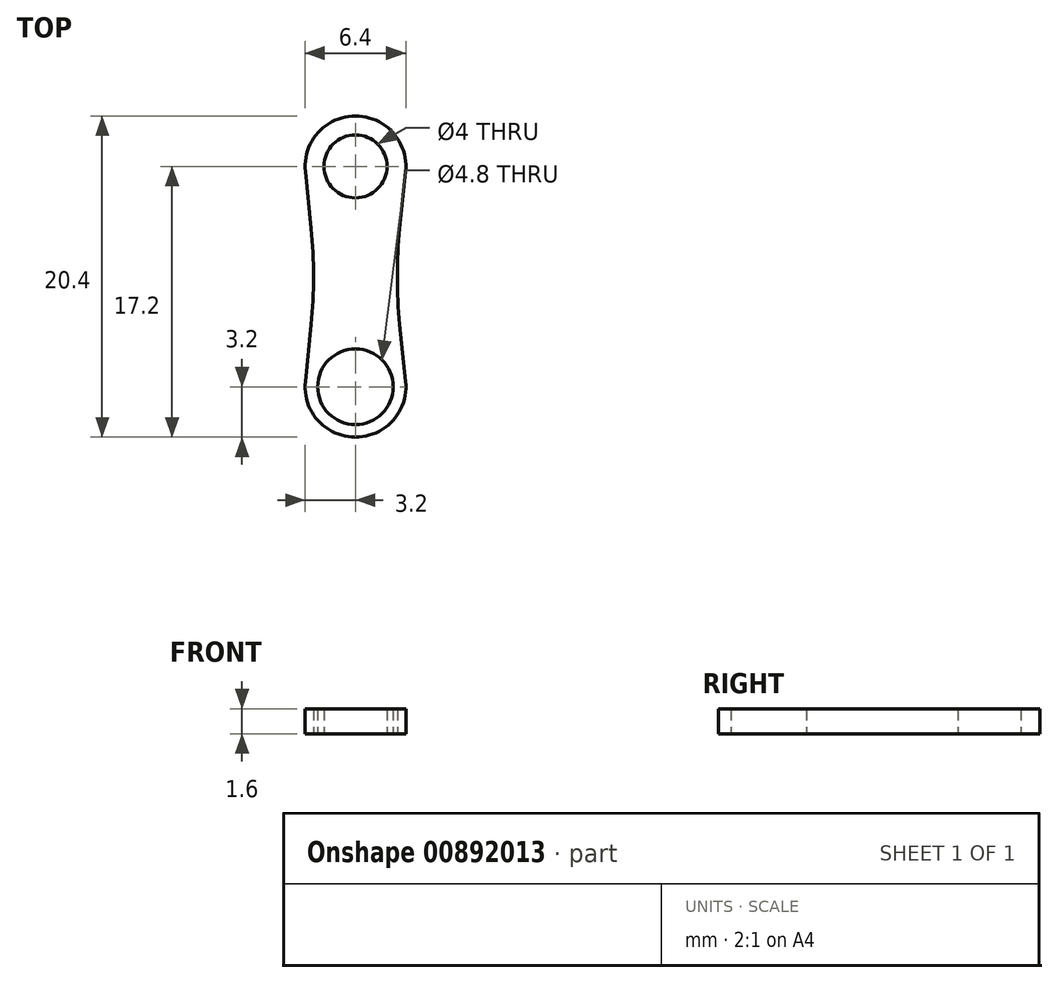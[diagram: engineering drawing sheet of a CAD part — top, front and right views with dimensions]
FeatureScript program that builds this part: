
annotation { "Feature Type Name" : "Feature", "Feature Type Description" : "" }
export const myFeature = defineFeature(function(context is Context, id is Id, definition is map)
    precondition{}
    {
        {
            var Q0;
            Q0=qCreatedBy(makeId("Top.planeOp"),FACE);
            var sketch = newSketch(context, id + "F0", { "sketchPlane" : qUnion([Q0])});
            skCircle(sketch, "E0", {"center": v(0, 0) * mm, "radius": 2.4 * mm});
            skLineSegment(sketch, "E1", {"start": v(0, 0) * mm, "end": v(0, 14) * mm});
            skCircle(sketch, "E2", {"center": v(0, 14) * mm, "radius": 2 * mm});
            skArc(sketch, "E3", {"start": v(-3.18, 0.33) * mm, "mid": v(0, -3.2) * mm, "end": v(3.18, 0.33) * mm});
            skArc(sketch, "E4", {"start": v(3.18, 13.67) * mm, "mid": v(0, 17.2) * mm, "end": v(-3.18, 13.67) * mm});
            skLineSegment(sketch, "E5", {"start": v(0, 7) * mm, "end": v(-2.5, 7) * mm});
            skLineSegment(sketch, "E6", {"start": v(-2.81, 3.94) * mm, "end": v(-3.18, 0.33) * mm});
            skLineSegment(sketch, "E7.MirrorCS", {"start": v(-2.81, 10.06) * mm, "end": v(-3.18, 13.67) * mm});
            skPoint(sketch, "E8.visualSharp", {"position": v(-2.5, 7) * mm});
            skArc(sketch, "E8.filletArc", {"start": v(-2.81, 3.94) * mm, "mid": v(-2.66, 7) * mm, "end": v(-2.81, 10.06) * mm});
            skLineSegment(sketch, "E9.MirrorCS", {"start": v(2.81, 10.06) * mm, "end": v(3.18, 13.67) * mm});
            skArc(sketch, "E10.MirrorCS", {"start": v(2.81, 3.94) * mm, "mid": v(2.66, 7) * mm, "end": v(2.81, 10.06) * mm});
            skLineSegment(sketch, "E11.MirrorCS", {"start": v(2.81, 3.94) * mm, "end": v(3.18, 0.33) * mm});
            skLineSegment(sketch, "E12", {"start": v(0, 7) * mm, "end": v(0, 12) * mm});
            skSolve(sketch);
        }
        {
            var Q0;
            Q0=qSketchRegion(id+"F0",true);
            extrude(context, id + "F1", {"entities" : qUnion([Q0]), "depth" : 1.6 * mm, "offsetDistance" : 25 * mm});
        }
    });
